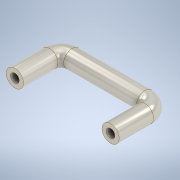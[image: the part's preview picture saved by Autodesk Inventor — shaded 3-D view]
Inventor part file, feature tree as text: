
AUTODESK INVENTOR PART (.ipt)
format: ipt  version: 2021 (Build 250183000, 183)  size: 151,040 bytes
history: native  units: in
note: dims shown in document units (in); Inventor stores cm internally (conversion verified against a paired STEP export)
features: sketch x2, sweep x1
ambient origin geometry x8: Origin, YZ Plane, XZ Plane, XY Plane, X Axis, Y Axis, Z Axis, Center Point
bodies: Solid1 (feature_tree)
feature tree (3):
  sweep  "Sweep1"
  sketch  "Sketch1"  dims[d4=0.1181in d5=0.0591in d6=0.315in d7=0.6567in d8=0.315in d9=0.0787in d10=0.0787in d11=0.0in d12=0.0in]
  sketch  "3D Sketch1"
